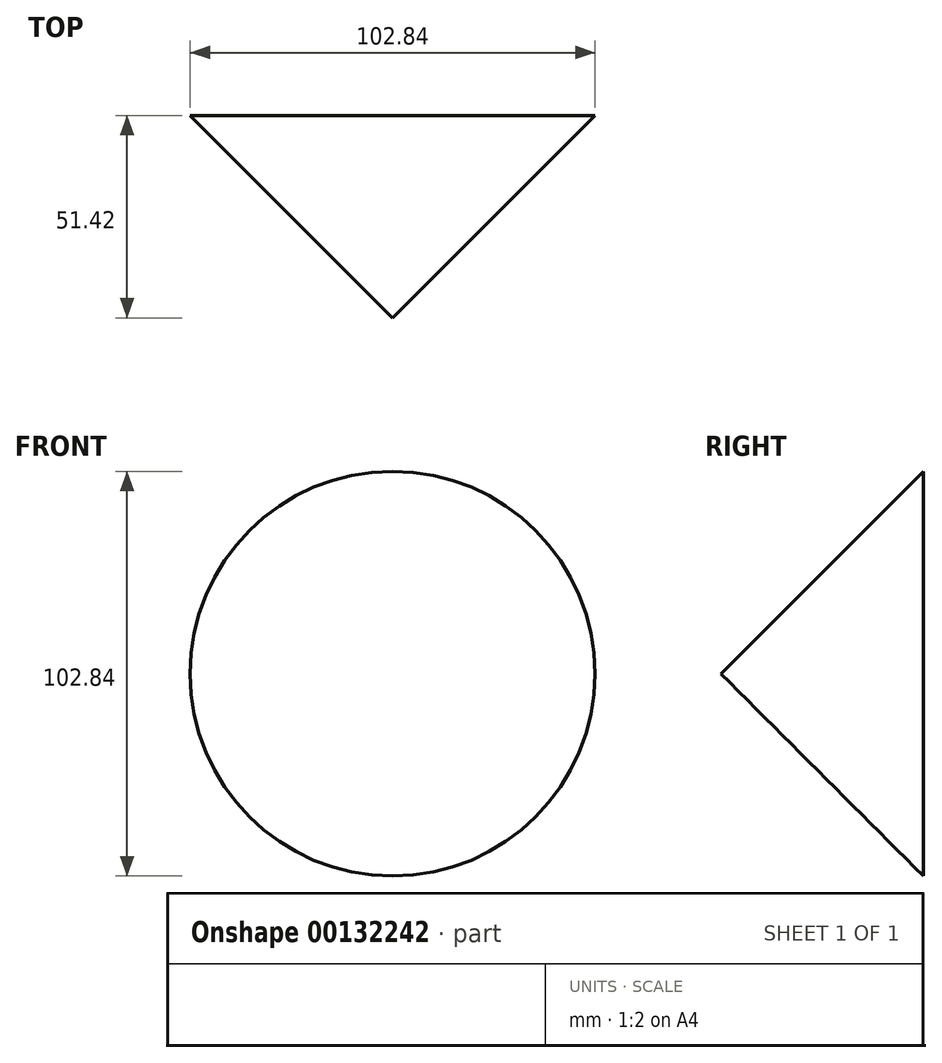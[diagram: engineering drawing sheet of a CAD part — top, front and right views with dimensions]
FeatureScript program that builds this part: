
annotation { "Feature Type Name" : "Feature", "Feature Type Description" : "" }
export const myFeature = defineFeature(function(context is Context, id is Id, definition is map)
    precondition{}
    {
        {
            var Q0;
            Q0=qCreatedBy(makeId("Front.planeOp"),FACE);
            var sketch = newSketch(context, id + "F0", { "sketchPlane" : qUnion([Q0])});
            skCircle(sketch, "E0", {"center": v(0, -2.18) * mm, "radius": 51.42 * mm});
            skSolve(sketch);
        }
        {
            var Q0;
            Q0 = qSketchRegion(id + "F0", true);
            extrude(context, id + "F1", {"entities" : qUnion([Q0]), "depth" : 254 * mm, "hasDraft" : true, "draftAngle" : 45 * degree, "draftPullDirection" : true});
        }
    });
